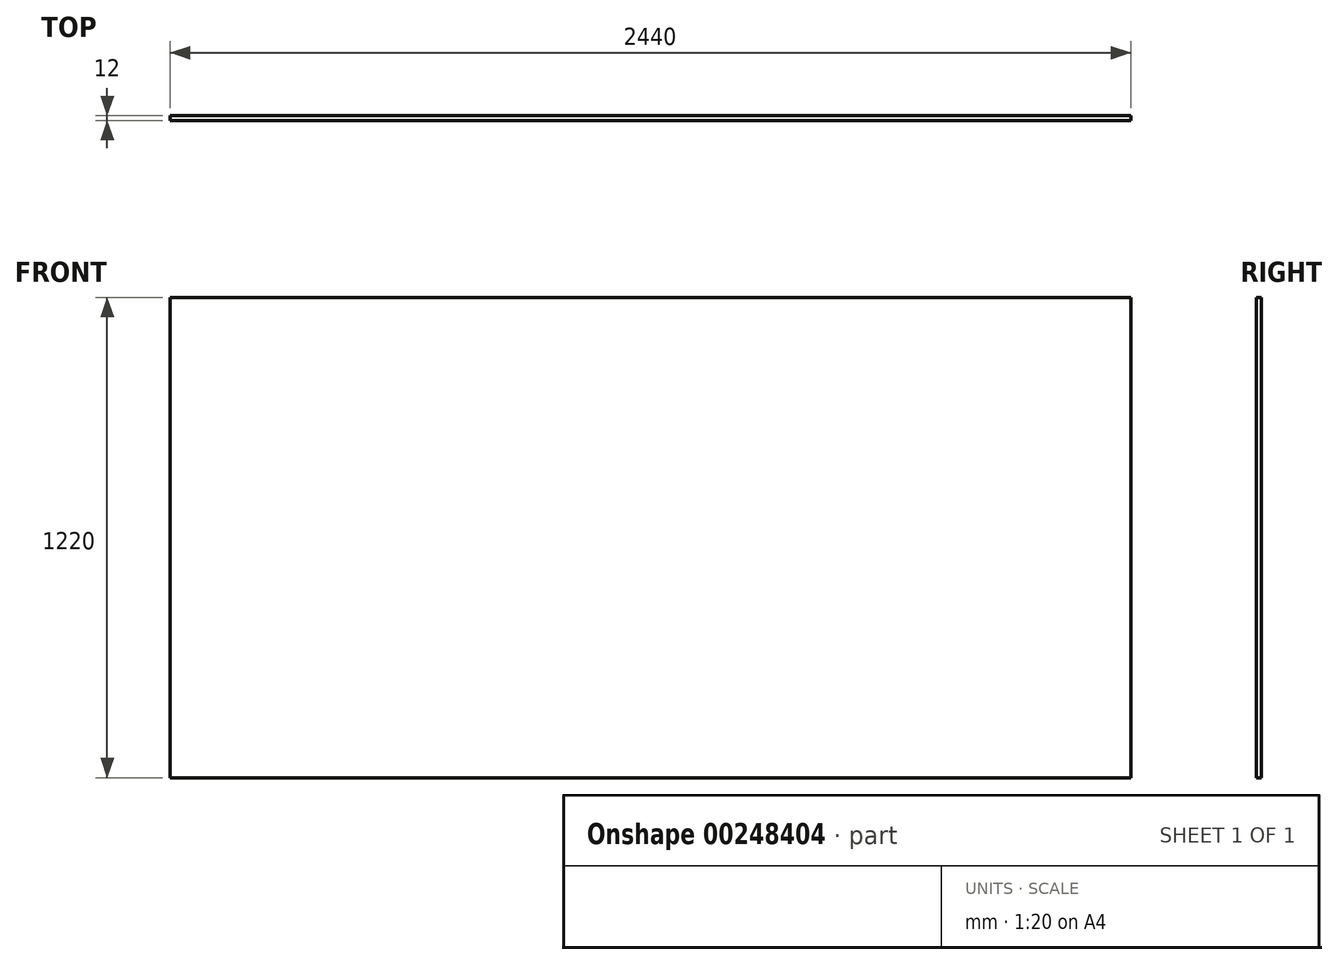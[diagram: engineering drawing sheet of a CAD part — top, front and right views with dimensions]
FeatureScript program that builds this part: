
annotation { "Feature Type Name" : "Feature", "Feature Type Description" : "" }
export const myFeature = defineFeature(function(context is Context, id is Id, definition is map)
    precondition{}
    {
        {
            var Q0;
            Q0=qCreatedBy(makeId("Front.planeOp"),FACE);
            var sketch = newSketch(context, id + "F0", { "sketchPlane" : qUnion([Q0])});
            skLineSegment(sketch, "E0.bottom", {"start": v(-1219.3, 530) * mm, "end": v(1220.7, 530) * mm});
            skLineSegment(sketch, "E0.top", {"start": v(-1219.3, -690) * mm, "end": v(1220.7, -690) * mm});
            skLineSegment(sketch, "E0.left", {"start": v(-1219.3, 530) * mm, "end": v(-1219.3, -690) * mm});
            skLineSegment(sketch, "E0.right", {"start": v(1220.7, 530) * mm, "end": v(1220.7, -690) * mm});
            skSolve(sketch);
        }
        {
            var Q0;
            Q0=makeQuery(id+"F0.imprint","IMPRINT",FACE,{"disambiguationData":[TD([[makeQuery(id+"F0.imprint","IMPRINT",EDGE,{"derivedFrom":sQuery(id+"F0.wireOp",EDGE,"E0.bottom")}),-1.0]])]});
            extrude(context, id + "F1", {"entities" : qUnion([Q0]), "depth" : 12 * mm});
        }
    });
